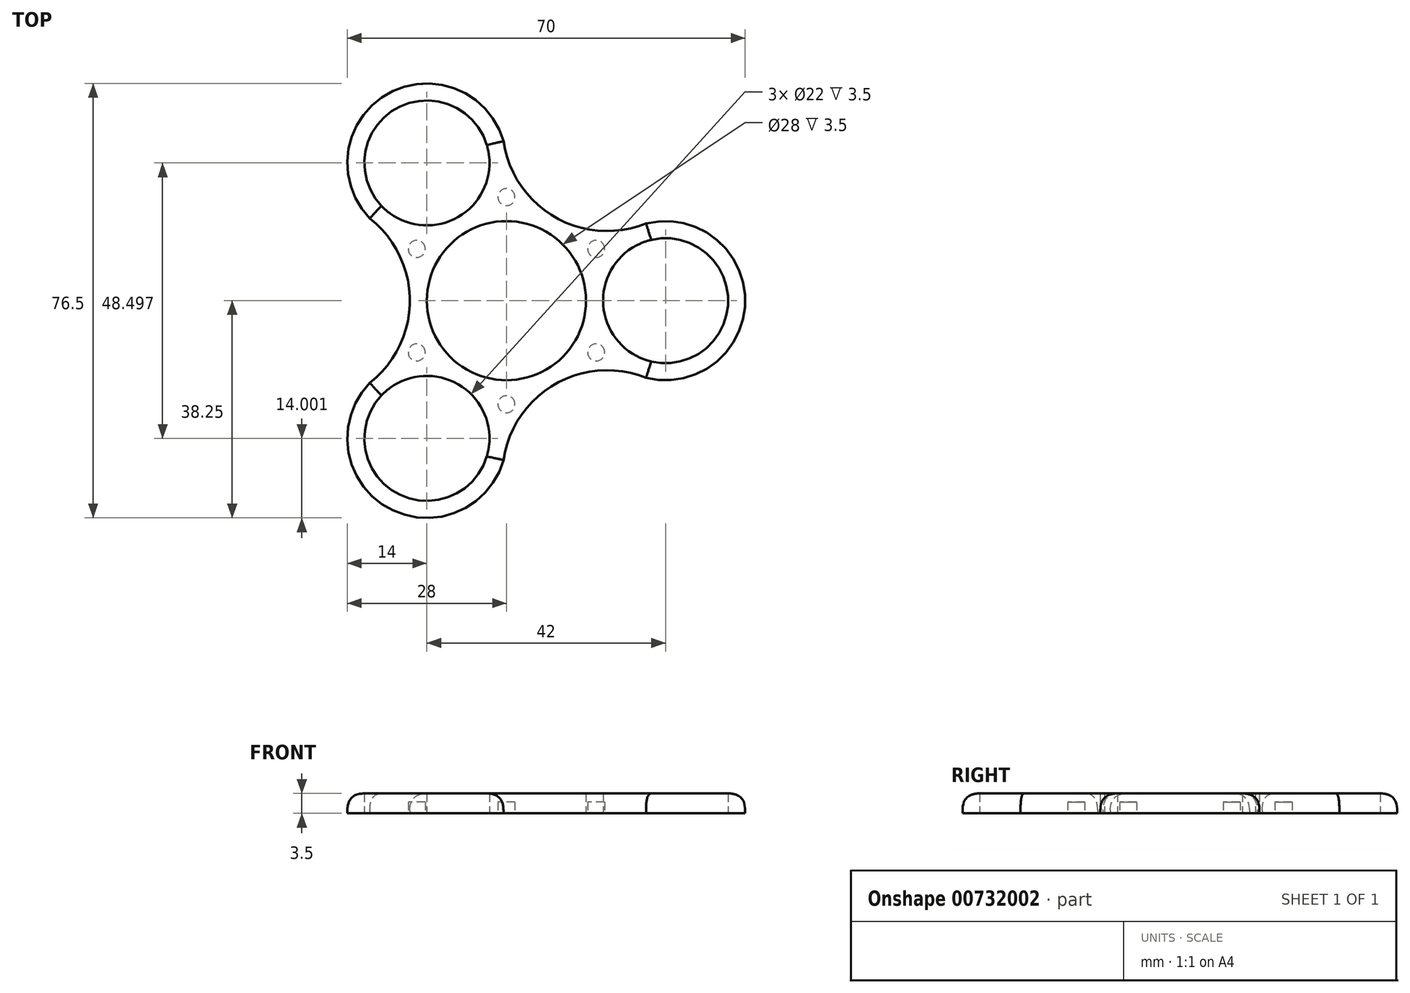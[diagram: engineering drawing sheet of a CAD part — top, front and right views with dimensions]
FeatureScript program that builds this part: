
annotation { "Feature Type Name" : "Feature", "Feature Type Description" : "" }
export const myFeature = defineFeature(function(context is Context, id is Id, definition is map)
    precondition{}
    {
        {
            var Q0;
            Q0=qCreatedBy(makeId("Top.planeOp"),FACE);
            var sketch = newSketch(context, id + "F0", { "sketchPlane" : qUnion([Q0])});
            skCircle(sketch, "E0", {"center": v(0, 0) * mm, "radius": 14 * mm});
            skLineSegment(sketch, "E1", {"start": v(14, 0) * mm, "end": v(17, 0) * mm});
            skLineSegment(sketch, "E2", {"start": v(17, 0) * mm, "end": v(28, 0) * mm});
            skCircle(sketch, "E3", {"center": v(28, 0) * mm, "radius": 11 * mm});
            skArc(sketch, "E4", {"start": v(22.57, -12.9) * mm, "mid": v(42, 0) * mm, "end": v(22.57, 12.9) * mm});
            skArc(sketch, "E5", {"start": v(-24.03, -14.48) * mm, "mid": v(-17, 0) * mm, "end": v(-24.03, 14.48) * mm});
            skArc(sketch, "E6.1.0", {"start": v(24.56, -13.57) * mm, "mid": v(8.5, -14.72) * mm, "end": v(-0.53, -28.05) * mm});
            skArc(sketch, "E6.1.1", {"start": v(-0.1, 26) * mm, "mid": v(-21, 36.37) * mm, "end": v(-22.46, 13.1) * mm});
            skCircle(sketch, "E6.1.2", {"center": v(-14, 24.25) * mm, "radius": 11 * mm});
            skArc(sketch, "E6.2.0", {"start": v(-0.53, 28.05) * mm, "mid": v(8.5, 14.72) * mm, "end": v(24.56, 13.57) * mm});
            skArc(sketch, "E6.2.1", {"start": v(-22.46, -13.1) * mm, "mid": v(-21, -36.37) * mm, "end": v(-0.1, -26) * mm});
            skCircle(sketch, "E6.2.2", {"center": v(-14, -24.25) * mm, "radius": 11 * mm});
            skSolve(sketch);
        }
        {
            var Q0;
            Q0=makeQuery(id+"F0.imprint","IMPRINT",FACE,{"disambiguationData":[TD([[makeQuery(id+"F0.imprint","IMPRINT",EDGE,{"derivedFrom":sQuery(id+"F0.wireOp",EDGE,"E0")}),-1.0]])]});
            extrude(context, id + "F1", {"entities" : qUnion([Q0]), "depth" : 3.5 * mm, "offsetDistance" : 25 * mm});
        }
        {
            var Q0;
            Q0=makeQuery(id+"F1.opExtrude","CAP_EDGE",EDGE,{"disambiguationData":[OSD([sQuery(id+"F0.wireOp",EDGE,"E6.1.0")])],"isStart":false});
            var Q1;
            Q1=makeQuery(id+"F1.opExtrude","CAP_EDGE",EDGE,{"disambiguationData":[OSD([sQuery(id+"F0.wireOp",EDGE,"E5")])],"isStart":false});
            var Q2;
            Q2=makeQuery(id+"F1.opExtrude","CAP_EDGE",EDGE,{"disambiguationData":[OSD([sQuery(id+"F0.wireOp",EDGE,"E6.2.0")])],"isStart":false});
            var Q3;
            Q3=makeQuery(id+"F1.opExtrude","CAP_EDGE",EDGE,{"disambiguationData":[OSD([sQuery(id+"F0.wireOp",EDGE,"E6.2.1")])],"isStart":false});
            var Q4;
            Q4=makeQuery(id+"F1.opExtrude","CAP_EDGE",EDGE,{"disambiguationData":[OSD([sQuery(id+"F0.wireOp",EDGE,"E4")])],"isStart":false});
            var Q5;
            Q5=makeQuery(id+"F1.opExtrude","CAP_EDGE",EDGE,{"disambiguationData":[OSD([sQuery(id+"F0.wireOp",EDGE,"E6.1.1")])],"isStart":false});
            fillet(context, id + "F2", {"entities" : qUnion([Q0, Q1, Q2, Q3, Q4, Q5]), "radius" : 3 * mm, "rho" : 0.5, "crossSection" : FilletCrossSection.CONIC, "allowEdgeOverflow" : false});
        }
        {
            var Q0;
            Q0=qCreatedBy(makeId("Top.planeOp"),FACE);
            var sketch = newSketch(context, id + "F3", { "sketchPlane" : qUnion([Q0])});
            skLineSegment(sketch, "E7.5", {"start": v(0, 18.23) * mm, "end": v(15.79, 9.12) * mm});
            skCircle(sketch, "E8", {"center": v(0, 18.23) * mm, "radius": 1.5 * mm});
            skCircle(sketch, "E9.1.0", {"center": v(-15.79, 9.12) * mm, "radius": 1.5 * mm});
            skLineSegment(sketch, "E9.1.1", {"start": v(-15.79, 9.12) * mm, "end": v(0, 18.23) * mm});
            skCircle(sketch, "E9.2.0", {"center": v(-15.79, -9.12) * mm, "radius": 1.5 * mm});
            skLineSegment(sketch, "E9.2.1", {"start": v(-15.79, -9.12) * mm, "end": v(-15.79, 9.12) * mm});
            skPoint(sketch, "E9.center", {"position": v(0, 0) * mm});
            skCircle(sketch, "E10.1.3.0", {"center": v(0, -18.23) * mm, "radius": 1.5 * mm});
            skLineSegment(sketch, "E10.2.3.0", {"start": v(0, -18.23) * mm, "end": v(-15.79, -9.12) * mm});
            skCircle(sketch, "E10.1.4.0", {"center": v(15.79, -9.12) * mm, "radius": 1.5 * mm});
            skLineSegment(sketch, "E10.2.4.0", {"start": v(15.79, -9.12) * mm, "end": v(0, -18.23) * mm});
            skCircle(sketch, "E10.1.5.0", {"center": v(15.79, 9.12) * mm, "radius": 1.5 * mm});
            skLineSegment(sketch, "E10.2.5.0", {"start": v(15.79, 9.12) * mm, "end": v(15.79, -9.12) * mm});
            skSolve(sketch);
        }
        {
            var Q0;
            {var subQ0=sQuery(id+"F3.wireOp",EDGE,"E9.1.1");var subQ1=sQuery(id+"F3.wireOp",EDGE,"E7.5");var subQ2=makeQuery(id+"F3.imprint","INTERSECT",VERTEX,{"derivedFrom":[subQ1,subQ0]});Q0=makeQuery(id+"F3.imprint","IMPRINT",FACE,{"disambiguationData":[TD([[makeQuery(id+"F3.imprint","IMPRINT",EDGE,{"disambiguationData":[TD([[subQ2,-1.0]])],"derivedFrom":subQ1}),1.0]])]});}
            var Q1;
            {var subQ0=sQuery(id+"F3.wireOp",EDGE,"E9.1.1");var subQ1=sQuery(id+"F3.wireOp",EDGE,"E7.5");var subQ2=makeQuery(id+"F3.imprint","INTERSECT",VERTEX,{"derivedFrom":[subQ1,subQ0]});Q1=makeQuery(id+"F3.imprint","IMPRINT",FACE,{"disambiguationData":[TD([[makeQuery(id+"F3.imprint","IMPRINT",EDGE,{"disambiguationData":[TD([[subQ2,-1.0]])],"derivedFrom":subQ1}),-1.0]])]});}
            var Q2;
            {var subQ0=sQuery(id+"F3.wireOp",EDGE,"E9.1.1");var subQ1=sQuery(id+"F3.wireOp",EDGE,"E9.1.0");var subQ2=makeQuery(id+"F3.imprint","INTERSECT",VERTEX,{"derivedFrom":[subQ1,subQ0]});Q2=makeQuery(id+"F3.imprint","IMPRINT",FACE,{"disambiguationData":[TD([[makeQuery(id+"F3.imprint","IMPRINT",EDGE,{"disambiguationData":[TD([[subQ2,-1.0]])],"derivedFrom":subQ1}),1.0]])]});}
            var Q3;
            {var subQ0=sQuery(id+"F3.wireOp",EDGE,"E9.1.1");var subQ1=sQuery(id+"F3.wireOp",EDGE,"E9.1.0");var subQ2=makeQuery(id+"F3.imprint","INTERSECT",VERTEX,{"derivedFrom":[subQ1,subQ0]});Q3=makeQuery(id+"F3.imprint","IMPRINT",FACE,{"disambiguationData":[TD([[makeQuery(id+"F3.imprint","IMPRINT",EDGE,{"disambiguationData":[TD([[subQ2,1.0]])],"derivedFrom":subQ1}),1.0]])]});}
            var Q4;
            {var subQ0=sQuery(id+"F3.wireOp",EDGE,"E10.2.5.0");var subQ1=sQuery(id+"F3.wireOp",EDGE,"E7.5");var subQ2=makeQuery(id+"F3.imprint","INTERSECT",VERTEX,{"derivedFrom":[subQ1,subQ0]});Q4=makeQuery(id+"F3.imprint","IMPRINT",FACE,{"disambiguationData":[TD([[makeQuery(id+"F3.imprint","IMPRINT",EDGE,{"disambiguationData":[TD([[subQ2,1.0]])],"derivedFrom":subQ1}),1.0]])]});}
            var Q5;
            {var subQ0=sQuery(id+"F3.wireOp",EDGE,"E10.2.5.0");var subQ1=sQuery(id+"F3.wireOp",EDGE,"E7.5");var subQ2=makeQuery(id+"F3.imprint","INTERSECT",VERTEX,{"derivedFrom":[subQ1,subQ0]});Q5=makeQuery(id+"F3.imprint","IMPRINT",FACE,{"disambiguationData":[TD([[makeQuery(id+"F3.imprint","IMPRINT",EDGE,{"disambiguationData":[TD([[subQ2,1.0]])],"derivedFrom":subQ1}),-1.0]])]});}
            var Q6;
            {var subQ0=sQuery(id+"F3.wireOp",EDGE,"E10.2.3.0");var subQ1=sQuery(id+"F3.wireOp",EDGE,"E10.1.3.0");var subQ2=makeQuery(id+"F3.imprint","INTERSECT",VERTEX,{"derivedFrom":[subQ1,subQ0]});Q6=makeQuery(id+"F3.imprint","IMPRINT",FACE,{"disambiguationData":[TD([[makeQuery(id+"F3.imprint","IMPRINT",EDGE,{"disambiguationData":[TD([[subQ2,-1.0]])],"derivedFrom":subQ1}),1.0]])]});}
            var Q7;
            {var subQ0=sQuery(id+"F3.wireOp",EDGE,"E10.2.3.0");var subQ1=sQuery(id+"F3.wireOp",EDGE,"E10.1.3.0");var subQ2=makeQuery(id+"F3.imprint","INTERSECT",VERTEX,{"derivedFrom":[subQ1,subQ0]});Q7=makeQuery(id+"F3.imprint","IMPRINT",FACE,{"disambiguationData":[TD([[makeQuery(id+"F3.imprint","IMPRINT",EDGE,{"disambiguationData":[TD([[subQ2,1.0]])],"derivedFrom":subQ1}),1.0]])]});}
            var Q8;
            {var subQ0=sQuery(id+"F3.wireOp",EDGE,"E9.2.1");var subQ1=sQuery(id+"F3.wireOp",EDGE,"E9.2.0");var subQ2=makeQuery(id+"F3.imprint","INTERSECT",VERTEX,{"derivedFrom":[subQ1,subQ0]});Q8=makeQuery(id+"F3.imprint","IMPRINT",FACE,{"disambiguationData":[TD([[makeQuery(id+"F3.imprint","IMPRINT",EDGE,{"disambiguationData":[TD([[subQ2,1.0]])],"derivedFrom":subQ1}),1.0]])]});}
            var Q9;
            {var subQ0=sQuery(id+"F3.wireOp",EDGE,"E9.2.1");var subQ1=sQuery(id+"F3.wireOp",EDGE,"E9.2.0");var subQ2=makeQuery(id+"F3.imprint","INTERSECT",VERTEX,{"derivedFrom":[subQ1,subQ0]});Q9=makeQuery(id+"F3.imprint","IMPRINT",FACE,{"disambiguationData":[TD([[makeQuery(id+"F3.imprint","IMPRINT",EDGE,{"disambiguationData":[TD([[subQ2,-1.0]])],"derivedFrom":subQ1}),1.0]])]});}
            var Q10;
            {var subQ0=sQuery(id+"F3.wireOp",EDGE,"E10.2.4.0");var subQ1=sQuery(id+"F3.wireOp",EDGE,"E10.1.4.0");var subQ2=makeQuery(id+"F3.imprint","INTERSECT",VERTEX,{"derivedFrom":[subQ1,subQ0]});Q10=makeQuery(id+"F3.imprint","IMPRINT",FACE,{"disambiguationData":[TD([[makeQuery(id+"F3.imprint","IMPRINT",EDGE,{"disambiguationData":[TD([[subQ2,1.0]])],"derivedFrom":subQ1}),1.0]])]});}
            var Q11;
            {var subQ0=sQuery(id+"F3.wireOp",EDGE,"E10.2.4.0");var subQ1=sQuery(id+"F3.wireOp",EDGE,"E10.1.4.0");var subQ2=makeQuery(id+"F3.imprint","INTERSECT",VERTEX,{"derivedFrom":[subQ1,subQ0]});Q11=makeQuery(id+"F3.imprint","IMPRINT",FACE,{"disambiguationData":[TD([[makeQuery(id+"F3.imprint","IMPRINT",EDGE,{"disambiguationData":[TD([[subQ2,-1.0]])],"derivedFrom":subQ1}),1.0]])]});}
            extrude(context, id + "F4", {"entities" : qUnion([Q0, Q1, Q2, Q3, Q4, Q5, Q6, Q7, Q8, Q9, Q10, Q11]), "operationType" : NewBodyOperationType.REMOVE, "depth" : 2 * mm, "offsetDistance" : 25 * mm});
        }
    });
